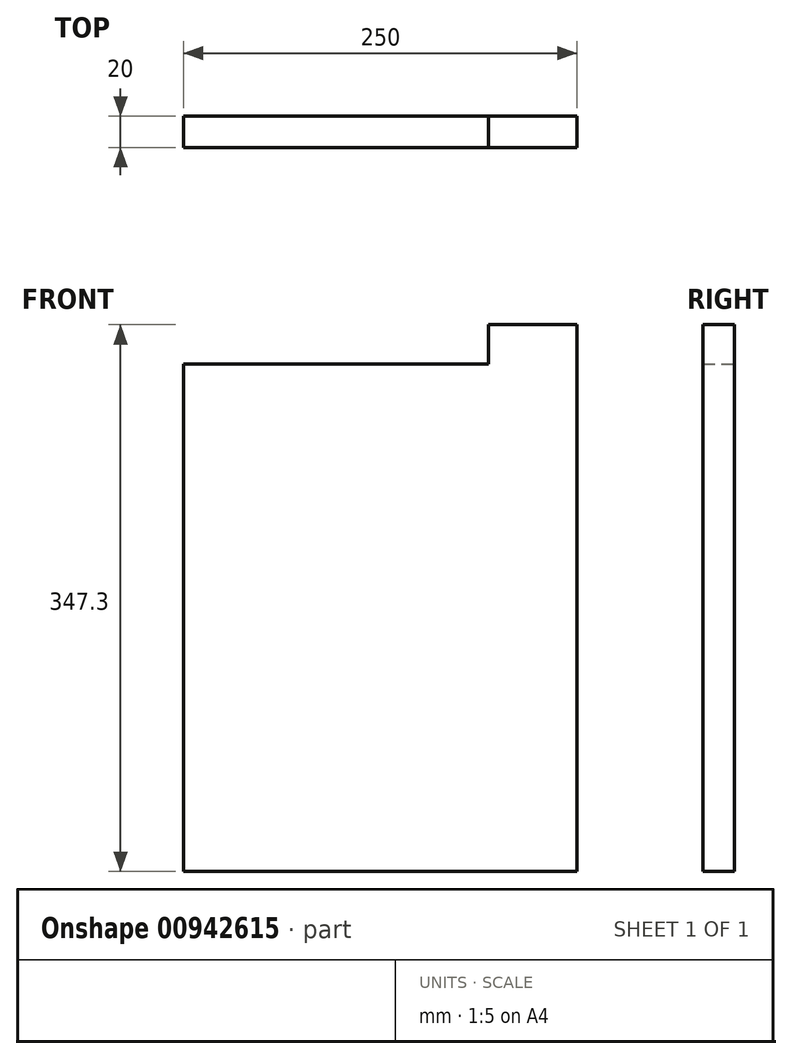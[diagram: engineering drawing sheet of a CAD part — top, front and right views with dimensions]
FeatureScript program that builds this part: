
annotation { "Feature Type Name" : "Feature", "Feature Type Description" : "" }
export const myFeature = defineFeature(function(context is Context, id is Id, definition is map)
    precondition{}
    {
        {
            var Q0;
            Q0=qCreatedBy(makeId("Front.planeOp"),FACE);
            var sketch = newSketch(context, id + "F0", { "sketchPlane" : qUnion([Q0])});
            skLineSegment(sketch, "E0.bottom", {"start": v(168.01, 320.19) * mm, "end": v(224.22, 320.19) * mm});
            skLineSegment(sketch, "E0.top", {"start": v(-25.78, -27.11) * mm, "end": v(224.22, -27.11) * mm});
            skLineSegment(sketch, "E0.left", {"start": v(-25.78, 295.19) * mm, "end": v(-25.78, -27.11) * mm});
            skLineSegment(sketch, "E0.right", {"start": v(224.22, 320.19) * mm, "end": v(224.22, -27.11) * mm});
            skLineSegment(sketch, "E1.top", {"start": v(-25.78, 295.19) * mm, "end": v(168.01, 295.19) * mm});
            skLineSegment(sketch, "E1.right", {"start": v(168.01, 320.19) * mm, "end": v(168.01, 295.19) * mm});
            skSolve(sketch);
        }
        {
            var Q0;
            Q0 = qSketchRegion(id + "F0", true);
            extrude(context, id + "F1", {"entities" : qUnion([Q0]), "depth" : 20 * mm, "offsetDistance" : 25 * mm});
        }
    });
